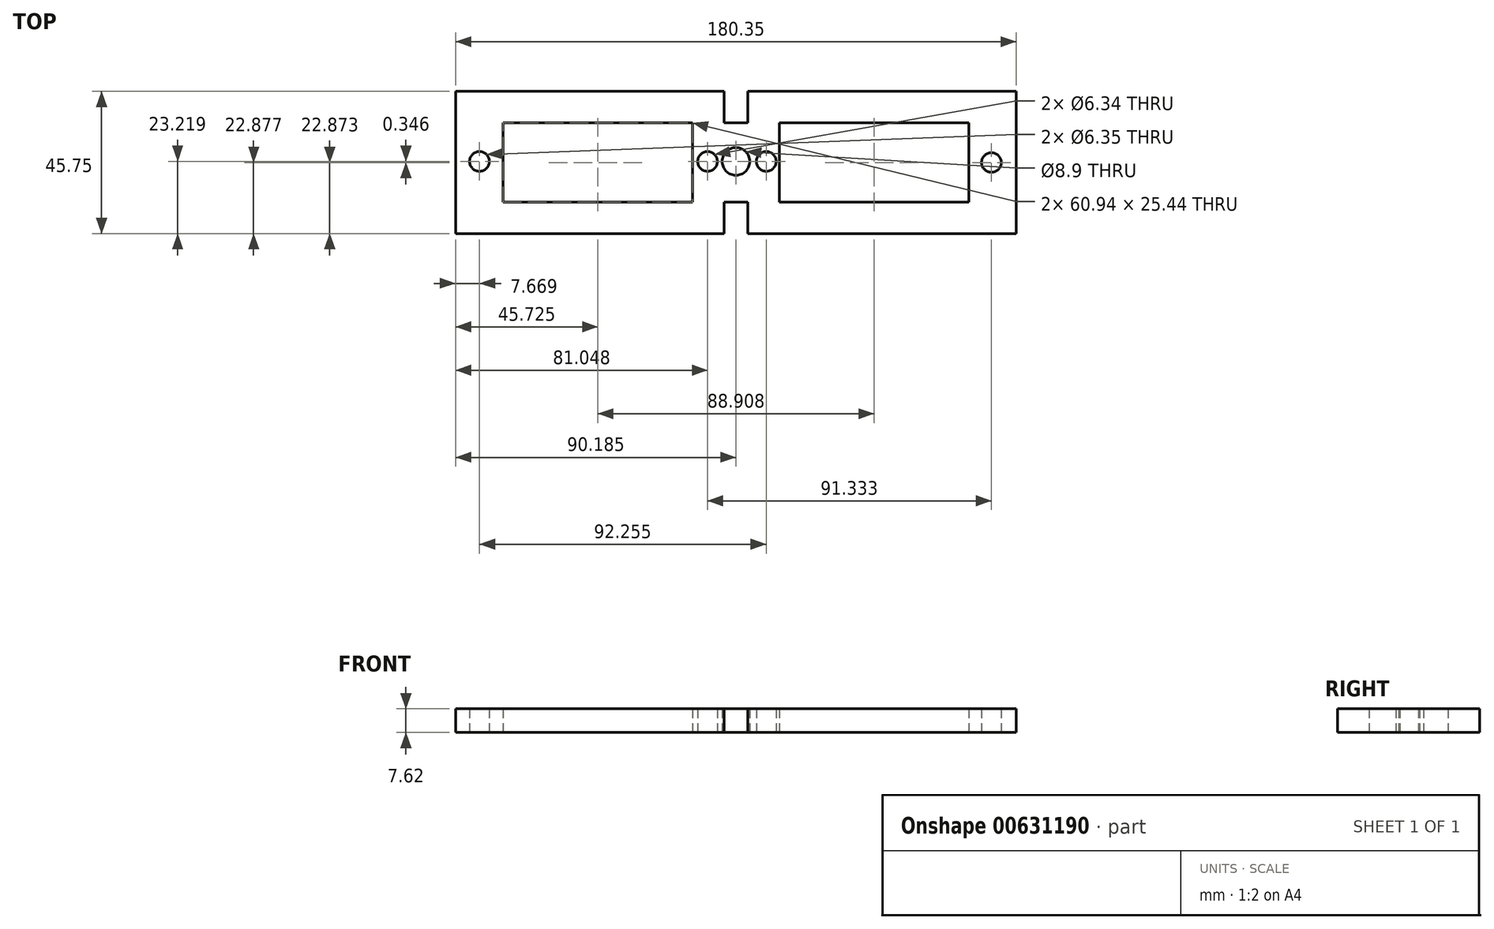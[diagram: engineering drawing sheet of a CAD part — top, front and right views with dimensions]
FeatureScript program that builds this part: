
annotation { "Feature Type Name" : "Feature", "Feature Type Description" : "" }
export const myFeature = defineFeature(function(context is Context, id is Id, definition is map)
    precondition{}
    {
        {
            var Q0;
            Q0=qCreatedBy(makeId("Top.planeOp"),FACE);
            var sketch = newSketch(context, id + "F0", { "sketchPlane" : qUnion([Q0])});
            skLineSegment(sketch, "E0", {"start": v(0, 0) * mm, "end": v(-86.35, 0) * mm});
            skLineSegment(sketch, "E1", {"start": v(-86.35, 0) * mm, "end": v(-86.35, -10.15) * mm});
            skLineSegment(sketch, "E2", {"start": v(-86.35, -10.15) * mm, "end": v(-93.98, -10.15) * mm});
            skLineSegment(sketch, "E3", {"start": v(-93.98, -10.15) * mm, "end": v(-93.98, 0) * mm});
            skLineSegment(sketch, "E4", {"start": v(-93.98, 0) * mm, "end": v(-180.35, 0) * mm});
            skLineSegment(sketch, "E5", {"start": v(-180.35, 0) * mm, "end": v(-180.35, -45.75) * mm});
            skLineSegment(sketch, "E6", {"start": v(-180.35, -45.75) * mm, "end": v(-93.98, -45.75) * mm});
            skLineSegment(sketch, "E7", {"start": v(-93.98, -45.75) * mm, "end": v(-93.98, -35.6) * mm});
            skLineSegment(sketch, "E8", {"start": v(-93.98, -35.6) * mm, "end": v(-86.35, -35.6) * mm});
            skLineSegment(sketch, "E9", {"start": v(-86.35, -35.6) * mm, "end": v(-86.35, -45.75) * mm});
            skLineSegment(sketch, "E10", {"start": v(-86.35, -45.75) * mm, "end": v(0, -45.75) * mm});
            skLineSegment(sketch, "E11", {"start": v(0, -45.75) * mm, "end": v(0, 0) * mm});
            skLineSegment(sketch, "E12", {"start": v(-180.35, 0) * mm, "end": v(-180.35, -10.15) * mm});
            skLineSegment(sketch, "E13", {"start": v(-180.35, -10.15) * mm, "end": v(-180.35, -35.6) * mm});
            skLineSegment(sketch, "E14", {"start": v(0, 0) * mm, "end": v(0, -10.15) * mm});
            skLineSegment(sketch, "E15", {"start": v(0, -10.15) * mm, "end": v(0, -35.6) * mm});
            skPoint(sketch, "E15.endSnap0", {"position": v(0, -22.88) * mm});
            skLineSegment(sketch, "E16", {"start": v(-93.98, 0) * mm, "end": v(-104.15, 0) * mm});
            skLineSegment(sketch, "E17", {"start": v(-180.35, 0) * mm, "end": v(-170.22, 0) * mm});
            skLineSegment(sketch, "E18", {"start": v(-180.35, -45.75) * mm, "end": v(-170.22, -45.75) * mm});
            skLineSegment(sketch, "E19", {"start": v(0, 0) * mm, "end": v(-10.16, 0) * mm});
            skLineSegment(sketch, "E20", {"start": v(0, -45.75) * mm, "end": v(-10.16, -45.75) * mm});
            skLineSegment(sketch, "E21", {"start": v(-86.35, 0) * mm, "end": v(-44.83, 0) * mm});
            skLineSegment(sketch, "E22", {"start": v(-86.35, 0) * mm, "end": v(-76.19, 0) * mm});
            skLineSegment(sketch, "E23", {"start": v(-86.35, -45.75) * mm, "end": v(-76.19, -45.75) * mm});
            skLineSegment(sketch, "E24", {"start": v(-180.35, 0) * mm, "end": v(-165.1, 0) * mm});
            skLineSegment(sketch, "E25", {"start": v(-180.35, -45.75) * mm, "end": v(-165.1, -45.75) * mm});
            skLineSegment(sketch, "E26", {"start": v(0, 0) * mm, "end": v(-15.25, 0) * mm});
            skLineSegment(sketch, "E27", {"start": v(0, -45.75) * mm, "end": v(-15.25, -45.75) * mm});
            skLineSegment(sketch, "E28", {"start": v(-15.25, -10.15) * mm, "end": v(-15.25, -35.6) * mm});
            skLineSegment(sketch, "E29", {"start": v(-15.25, -35.6) * mm, "end": v(-76.19, -35.6) * mm});
            skLineSegment(sketch, "E30", {"start": v(-76.19, -35.6) * mm, "end": v(-76.19, -10.15) * mm});
            skLineSegment(sketch, "E31", {"start": v(-76.19, -10.15) * mm, "end": v(-15.25, -10.15) * mm});
            skLineSegment(sketch, "E32", {"start": v(-165.1, -35.6) * mm, "end": v(-165.1, -10.15) * mm});
            skLineSegment(sketch, "E33", {"start": v(-165.1, -10.15) * mm, "end": v(-104.15, -10.15) * mm});
            skLineSegment(sketch, "E34", {"start": v(-104.15, -10.15) * mm, "end": v(-104.15, -35.6) * mm});
            skCircle(sketch, "E35", {"center": v(-90.16, -22.53) * mm, "radius": 4.45 * mm});
            skPoint(sketch, "E35.centerSnap0", {"position": v(-90.16, -10.15) * mm});
            skCircle(sketch, "E36", {"center": v(-99.3, -22.53) * mm, "radius": 3.17 * mm});
            skCircle(sketch, "E37", {"center": v(-80.43, -22.53) * mm, "radius": 3.18 * mm});
            skCircle(sketch, "E38", {"center": v(-7.97, -22.88) * mm, "radius": 3.17 * mm});
            skCircle(sketch, "E39", {"center": v(-172.68, -22.53) * mm, "radius": 3.18 * mm});
            skLineSegment(sketch, "E40", {"start": v(-165.1, -35.6) * mm, "end": v(-104.15, -35.6) * mm});
            skSolve(sketch);
        }
        {
            var Q0;
            Q0 = qSketchRegion(id + "F0", true);
            extrude(context, id + "F1", {"entities" : qUnion([Q0]), "depth" : 7.62 * mm, "offsetDistance" : 25.4 * mm});
        }
    });
